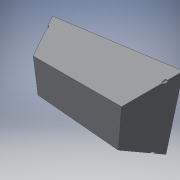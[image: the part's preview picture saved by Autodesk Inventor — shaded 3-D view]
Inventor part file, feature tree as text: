
AUTODESK INVENTOR PART (.ipt)
format: ipt  version: 2019 (Build 230136000, 136)  size: 160,256 bytes
history: native  units: in
note: dims shown in document units (in); Inventor stores cm internally (conversion verified against a paired STEP export)
features: sketch x5, plane x2, loft x2, extrude x1
ambient origin geometry x8: Origin, YZ Plane, XZ Plane, XY Plane, X Axis, Y Axis, Z Axis, Center Point
bodies: Solid1 (feature_tree)
feature tree (10):
  sketch  "Sketch1"  dims[d0=14.125in d1=8.25in]
  plane  "Work Plane1"
  loft  "Loft1"
  sketch  "Sketch3"  dims[d4=2.0in d5=0.0in d6=90.0deg]
  plane  "Work Plane2"
  loft  "Loft2"
  extrude  "Extrusion1"  TaperAngle=0.0deg  [1 undecoded]
  sketch  "Sketch2"  dims[d2=4.0in d3=2.0in]
  sketch  "Sketch5"  dims[d7=0.0in d8=90.0deg]
  sketch  "Sketch6"  dims[d9=0.125in d10=0.125in d11=1.0in d12=3.875in d15=0.125in d16=0.0in d17=90.0deg d18=0.0in d19=90.0deg d20=0.5in d21=0.5in d22=0.25in d23=1.0in d24=0.0in]
note: 1 required parameter value undecoded (feature->parameter linkage not recoverable at this tier; creation-order binding heuristic only, values carry confidence <= 0.55)
